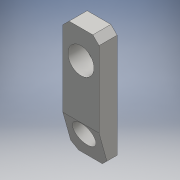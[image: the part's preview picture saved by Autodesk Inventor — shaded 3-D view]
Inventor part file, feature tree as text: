
AUTODESK INVENTOR PART (.ipt)
format: ipt  version: 2016 (Build 200138000, 138)  size: 131,584 bytes
history: native  units: mm
features: chamfer x4, sketch x4, extrude x3, hole x1, plane x1
ambient origin geometry x8: Origin, YZ Plane, XZ Plane, XY Plane, X Axis, Y Axis, Z Axis, Center Point
bodies: Solid1 (feature_tree)
feature tree (13):
  extrude  "Extrusion1"  Depth=20.6mm
  hole  "Hole1"  [1 undecoded]
  chamfer  "Chamfer1"  Distance=1.1mm Angle=45.0deg
  chamfer  "Chamfer2"  Distance=1.1mm Angle=45.0deg
  chamfer  "Chamfer3"  Distance=1.1mm Angle=45.0deg
  chamfer  "Chamfer4"  Distance=1.7mm
  sketch  "Sketch5"  dims[d4=4.6mm d5=6.0mm d6=4.0mm d7=2.0mm d8=90.0deg d9=8.0mm d10=20.594885mm d11=1.1mm d12=2.0mm d13=45.0deg d14=1.1mm d15=2.0mm d16=45.0deg d17=1.1mm d18=2.0mm d19=45.0deg d20=1.1mm d21=2.0mm d22=45.0deg]
  extrude  "Extrusion3"  Depth=10.0mm TaperAngle=0.0deg
  plane  "Work Plane1"
  extrude  "Extrusion4"  TaperAngle=0.0deg  [1 undecoded]
  sketch  "Sketch1"  dims[d0=6.4mm d1=20.6mm]
  sketch  "Sketch3"  dims[d2=3.2mm d3=0.0mm]
  sketch  "Sketch11"  dims[d26=6.1mm d27=1.7mm d28=10.0mm d29=0.0mm d30=0.0mm d31=4.02mm d32=4.2mm d33=0.0mm d34=2.1mm]
note: 2 required parameter values undecoded (feature->parameter linkage not recoverable at this tier; creation-order binding heuristic only, values carry confidence <= 0.55)
